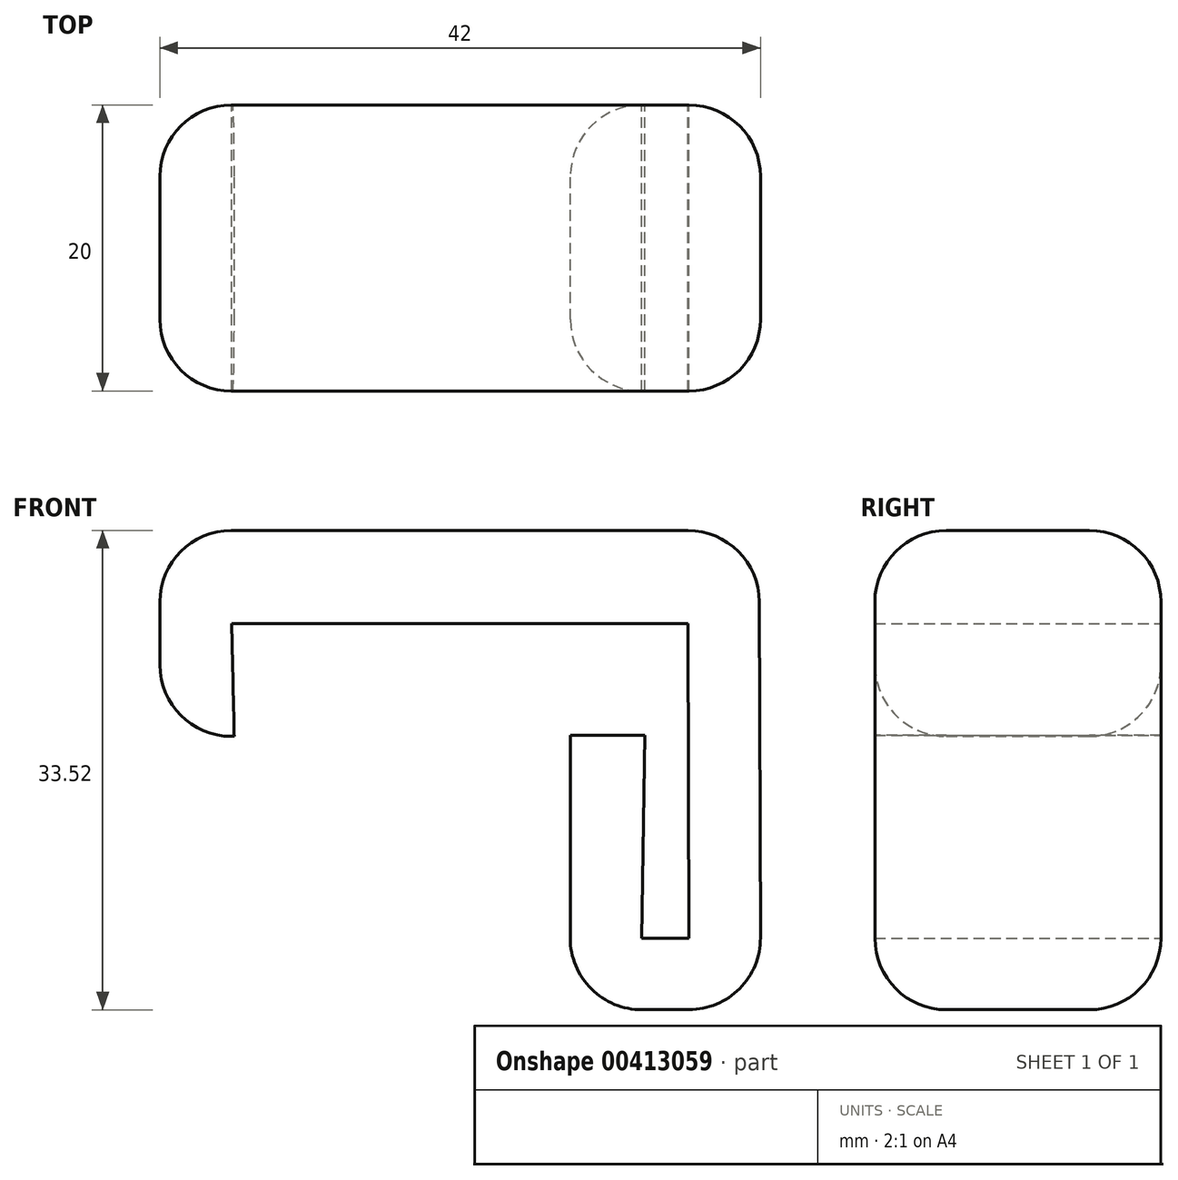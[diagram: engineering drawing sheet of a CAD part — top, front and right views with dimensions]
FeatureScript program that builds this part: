
annotation { "Feature Type Name" : "Feature", "Feature Type Description" : "" }
export const myFeature = defineFeature(function(context is Context, id is Id, definition is map)
    precondition{}
    {
        {
            var Q0;
            Q0=qCreatedBy(makeId("Front.planeOp"),FACE);
            var sketch = newSketch(context, id + "F0", { "sketchPlane" : qUnion([Q0])});
            skLineSegment(sketch, "E0", {"start": v(-23.13, 0.98) * mm, "end": v(-23.2, 22.98) * mm});
            skLineSegment(sketch, "E1", {"start": v(-23.2, 22.98) * mm, "end": v(-55.1, 22.98) * mm});
            skLineSegment(sketch, "E2", {"start": v(-18.23, 29.5) * mm, "end": v(-18.13, 1) * mm});
            skLineSegment(sketch, "E3.left", {"start": v(-55.1, 22.98) * mm, "end": v(-54.93, 15.1) * mm});
            skLineSegment(sketch, "E3.right", {"start": v(-60.13, 29.5) * mm, "end": v(-60.13, 15.1) * mm});
            skLineSegment(sketch, "E4.bottom", {"start": v(-23.13, 0.98) * mm, "end": v(-26.43, 0.97) * mm});
            skLineSegment(sketch, "E4.left", {"start": v(-18.13, 1) * mm, "end": v(-18.11, -4) * mm});
            skLineSegment(sketch, "E5.right", {"start": v(-31.43, -4.03) * mm, "end": v(-31.43, 15.17) * mm});
            skLineSegment(sketch, "E6", {"start": v(-60.13, 29.5) * mm, "end": v(-18.23, 29.5) * mm});
            skLineSegment(sketch, "E7", {"start": v(-54.93, 15.1) * mm, "end": v(-60.13, 15.1) * mm});
            skLineSegment(sketch, "E8", {"start": v(-31.43, -4.03) * mm, "end": v(-18.11, -4) * mm});
            skLineSegment(sketch, "E9", {"start": v(-31.43, 15.17) * mm, "end": v(-26.23, 15.17) * mm});
            skLineSegment(sketch, "E10", {"start": v(-26.43, 0.97) * mm, "end": v(-26.23, 15.17) * mm});
            skSolve(sketch);
        }
        {
            var Q0;
            Q0 = qSketchRegion(id + "F0", true);
            extrude(context, id + "F1", {"entities" : qUnion([Q0]), "depth" : 20 * mm});
        }
        {
            var Q0;
            Q0=makeQuery(id+"F1.opExtrude","SWEPT_EDGE",EDGE,{"disambiguationData":[OSD([sQuery(id+"F0.wireOp",EDGE,"TS6beSiI-nj1n-f17Q-Crop-148hrbHxsKN0"),sQuery(id+"F0.wireOp",EDGE,"E2")])]});
            var Q1;
            Q1=makeQuery(id+"F1.opExtrude","SWEPT_EDGE",EDGE,{"disambiguationData":[OSD([sQuery(id+"F0.wireOp",EDGE,"E3.bottom"),sQuery(id+"F0.wireOp",EDGE,"E3.right")])]});
            var Q2;
            Q2=makeQuery(id+"F1.opExtrude","SWEPT_EDGE",EDGE,{"disambiguationData":[OSD([sQuery(id+"F0.wireOp",EDGE,"E2"),sQuery(id+"F0.wireOp",EDGE,"IxrDtATP-84qB-ZlKZ-pPf0-4Rmvt9ccO3Vq")])]});
            var Q3;
            Q3=makeQuery(id+"F1.opExtrude","SWEPT_EDGE",EDGE,{"disambiguationData":[OSD([sQuery(id+"F0.wireOp",EDGE,"IxrDtATP-84qB-ZlKZ-pPf0-4Rmvt9ccO3Vq"),sQuery(id+"F0.wireOp",EDGE,"CmF1Wkn1-OxH5-R1yd-DDjo-RhM65i1EGk5q")])]});
            var Q4;
            Q4=makeQuery(id+"F1.opExtrude","SWEPT_EDGE",EDGE,{"disambiguationData":[OSD([sQuery(id+"F0.wireOp",EDGE,"E4.left"),sQuery(id+"F0.wireOp",EDGE,"E8")])]});
            var Q5;
            Q5=makeQuery(id+"F1.opExtrude","SWEPT_EDGE",EDGE,{"disambiguationData":[OSD([sQuery(id+"F0.wireOp",EDGE,"E5.right"),sQuery(id+"F0.wireOp",EDGE,"E8")])]});
            fillet(context, id + "F2", {"entities" : qUnion([Q0, Q1, Q2, Q3, Q4, Q5]), "radius" : 5 * mm, "tangentPropagation" : true, "allowEdgeOverflow" : false});
        }
        {
            var Q0;
            Q0=makeQuery(id+"F1.opExtrude","CAP_EDGE",EDGE,{"disambiguationData":[OSD([sQuery(id+"F0.wireOp",EDGE,"E6")])],"isStart":false});
            var Q1;
            Q1=makeQuery(id+"F1.opExtrude","CAP_EDGE",EDGE,{"disambiguationData":[OSD([sQuery(id+"F0.wireOp",EDGE,"E6")])],"isStart":true});
            fillet(context, id + "F3", {"entities" : qUnion([Q0, Q1]), "radius" : 5 * mm, "tangentPropagation" : true, "allowEdgeOverflow" : false});
        }
    });
